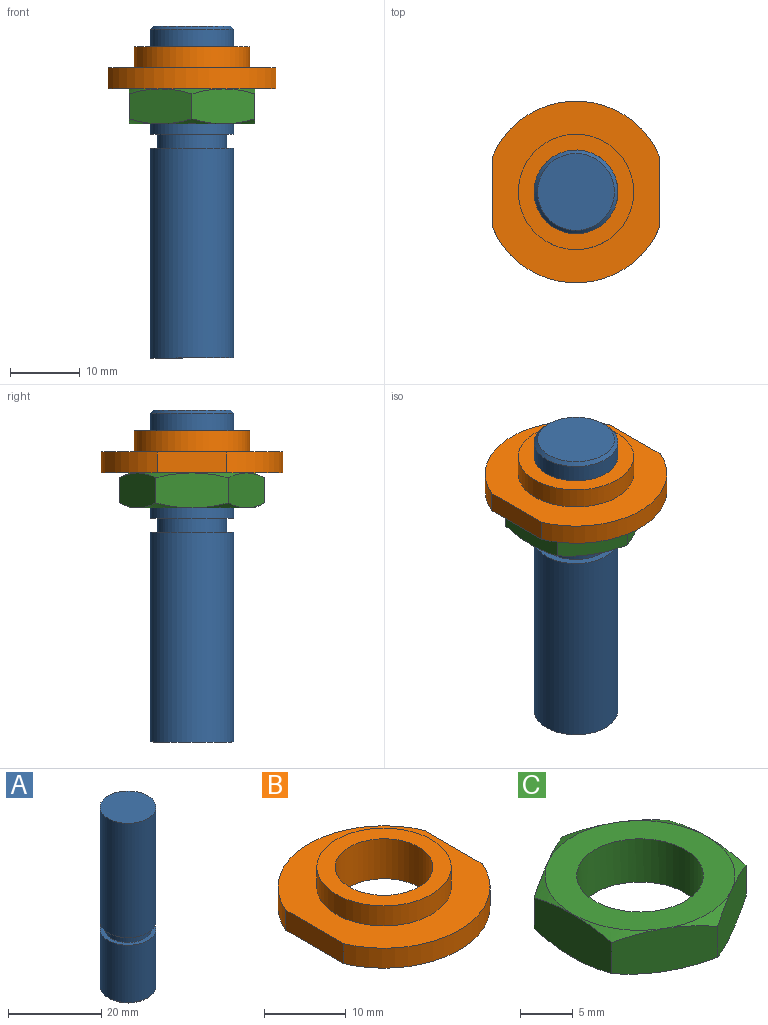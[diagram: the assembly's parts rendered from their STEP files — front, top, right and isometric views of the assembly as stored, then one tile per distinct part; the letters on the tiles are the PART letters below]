
ASSEMBLY  parts=3 mates=2
PART A: 8 faces, bbox 12x12x47.5 mm
  f0: plane 12x12mm, normal (0,0,1), area 113.1mm2, adj f6
  f1: plane 11x11mm, normal (0,0,-1), area 95mm2, adj f7
  f2: cylinder r=6mm len=15mm, axis (0,0,1), area 565.5mm2, adj f3,f7
  f3: plane 12x12mm, normal (0,0,1), area 34.6mm2, adj f2,f4
  f4: cylinder r=5mm len=10mm, axis (0,0,1), area 62.8mm2, adj f3,f5
  f5: plane 12x12mm, normal (0,0,-1), area 34.6mm2, adj f4,f6
  f6: cylinder r=6mm len=30mm, axis (0,0,1), area 1131mm2, adj f0,f5
  f7: cone r=6mm half-angle=45deg, axis (0,0,1), area 25.5mm2, adj f1,f2
PART B: 9 faces, bbox 24x26x6 mm
  f0: cylinder r=13mm len=24mm, axis (0,0,-1), area 91.7mm2, adj f1,f2,f7,f8
  f1: plane 26x24mm, normal (0,0,1), area 303.7mm2, adj f0,f4,f5,f7,f8
  f2: plane 26x24mm, normal (0,0,-1), area 404.4mm2, adj f0,f3,f4,f7,f8
  f3: cylinder r=6mm len=12mm, axis (0,0,-1), area 226.2mm2, adj f2,f6
  f4: cylinder r=13mm len=24mm, axis (0,0,-1), area 91.7mm2, adj f1,f2,f7,f8
  f5: cylinder r=8.25mm len=16.5mm, axis (0,0,-1), area 155.5mm2, adj f1,f6
  f6: plane 16.5x16.5mm, normal (0,0,1), area 100.7mm2, adj f3,f5
  f7: plane 10x3mm, normal (1,0,0), area 30mm2, adj f0,f1,f2,f4
  f8: plane 10x3mm, normal (-1,0,0), area 30mm2, adj f0,f1,f2,f4
PART C: 21 faces, bbox 20.8x20.8x5 mm
  f0: sphere r=21.36mm, area 4.9mm2, adj f12,f13,f19
  f1: sphere r=21.36mm, area 4.9mm2, adj f13,f14,f19
  f2: sphere r=21.36mm, area 4.9mm2, adj f14,f15,f19
  f3: sphere r=21.36mm, area 4.9mm2, adj f15,f17,f19
  f4: sphere r=21.36mm, area 4.9mm2, adj f16,f17,f19
  f5: sphere r=21.36mm, area 4.9mm2, adj f12,f16,f19
  f6: sphere r=21.36mm, area 4.9mm2, adj f14,f15,f18
  f7: sphere r=21.36mm, area 4.9mm2, adj f13,f14,f18
  f8: sphere r=21.36mm, area 4.9mm2, adj f12,f13,f18
  f9: sphere r=21.36mm, area 4.9mm2, adj f12,f16,f18
  f10: sphere r=21.36mm, area 4.9mm2, adj f16,f17,f18
  f11: sphere r=21.36mm, area 4.9mm2, adj f15,f17,f18
  f12: plane 10.39x5mm, normal (-1,0,0), area 47.1mm2, adj f0,f5,f8,f9,f13,f16
  f13: plane 9x5.2mm, normal (-0.5,-0.87,0), area 47.1mm2, adj f0,f1,f7,f8,f12,f14
  f14: plane 9x5.2mm, normal (0.5,-0.87,0), area 47.1mm2, adj f1,f2,f6,f7,f13,f15
  f15: plane 10.39x5mm, normal (1,0,0), area 47.1mm2, adj f2,f3,f6,f11,f14,f17
  f16: plane 9x5.2mm, normal (-0.5,0.87,0), area 47.1mm2, adj f4,f5,f9,f10,f12,f17
  f17: plane 9x5.2mm, normal (0.5,0.87,0), area 47.1mm2, adj f3,f4,f10,f11,f15,f16
  f18: plane 18x18mm, normal (0,0,1), area 141.4mm2, adj f6,f7,f8,f9,f10,f11,f20
  f19: plane 18x18mm, normal (0,0,-1), area 141.4mm2, adj f0,f1,f2,f3,f4,f5,f20
  f20: cylinder r=6mm len=12mm, axis (0,0,1), area 188.5mm2, adj f18,f19
PLACE A rot(axis=(0,1,0),180deg) t=(0,0,47.5)mm
PLACE B t=(0,0,38.5)mm
PLACE C t=(0,0,33.5)mm
MATE fastened C.f20 <-> B.f0  axis (0,0,1) through (0,0,38.5)mm
MATE fastened B.f0 <-> A.f2  axis (0,0,1) through (0,0,41.5)mm
